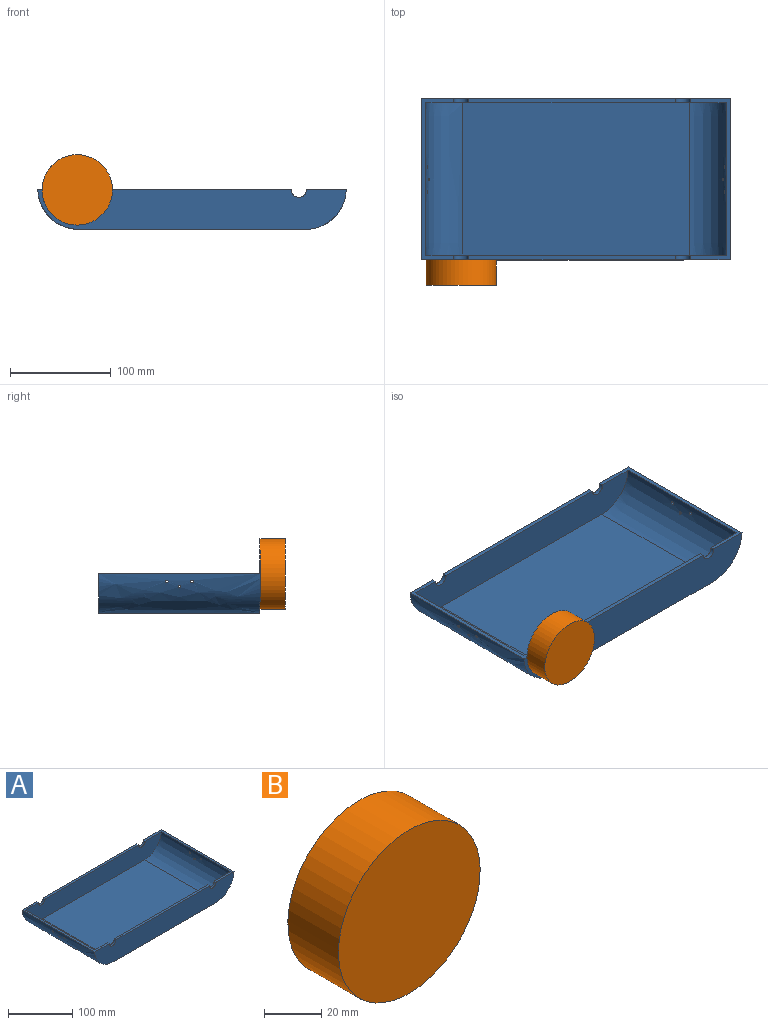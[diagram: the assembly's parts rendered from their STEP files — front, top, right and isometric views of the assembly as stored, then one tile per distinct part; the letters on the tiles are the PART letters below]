
ASSEMBLY  parts=2 mates=1
PART A: 24 faces, bbox 306.3x160.1x39.1 mm
  f0: cylinder r=7.5mm len=15mm, axis (0,-1,0), area 94mm2, adj f2,f7,f8,f13
  f1: cylinder r=7.5mm len=15mm, axis (0,-1,0), area 94mm2, adj f3,f7,f12,f17
  f2: plane 205.13x4.03mm, normal (0,0,1), area 820.5mm2, adj f0,f4,f8,f13
  f3: plane 205.13x4.03mm, normal (0,0,1), area 820.5mm2, adj f1,f5,f12,f17
  f4: cylinder r=7.5mm len=15mm, axis (0,-1,0), area 94.2mm2, adj f2,f6,f8,f13
  f5: cylinder r=7.5mm len=15mm, axis (0,-1,0), area 94.2mm2, adj f3,f6,f12,f17
  f6: plane 160.01x39.49mm, normal (0,0,1), area 924.2mm2, adj f4,f5,f8,f11,f12,f13,f16,f17
  f7: plane 160.01x31.69mm, normal (0,0,1), area 861.8mm2, adj f0,f1,f8,f9,f12,f13,f14,f17
  f8: plane 306.25x39.14mm, normal (0,1,0), area 11099.7mm2, adj f0,f2,f4,f6,f7,f9,f10,f11
  f9: extruded ~160.01x40.74mm, area 9968.4mm2, adj f7,f8,f10,f12,f21,f22,f23
  f10: plane 224.84x160.04mm, normal (0,0,-1), area 35970.4mm2, adj f8,f9,f11,f12
  f11: extruded ~160.01x40.74mm, area 9968.4mm2, adj f6,f8,f10,f12,f18,f19,f20
  f12: plane 306.25x39.14mm, normal (0,-1,0), area 11099.7mm2, adj f1,f3,f5,f6,f7,f9,f10,f11
  f13: plane 298.24x35.14mm, normal (0,-1,0), area 9726.1mm2, adj f0,f2,f4,f6,f7,f14,f15,f16
  f14: extruded ~152.01x36.74mm, area 8514mm2, adj f7,f13,f15,f17,f21,f22,f23
  f15: plane 224.84x152.04mm, normal (0,0,1), area 34171.9mm2, adj f13,f14,f16,f17
  f16: extruded ~152.01x36.74mm, area 8514mm2, adj f6,f13,f15,f17,f18,f19,f20
  f17: plane 298.24x35.14mm, normal (0,1,0), area 9726.2mm2, adj f1,f3,f5,f6,f7,f14,f15,f16
  f18: cylinder r=1.25mm len=4.73mm, axis (-1,0,0), area 32.3mm2, adj f11,f16
  f19: cylinder r=1.25mm len=5.28mm, axis (-1,0,0), area 33.8mm2, adj f11,f16
  f20: cylinder r=1.25mm len=4.73mm, axis (-1,0,0), area 32.3mm2, adj f11,f16
  f21: cylinder r=1.25mm len=4.73mm, axis (-1,0,0), area 32.3mm2, adj f9,f14
  f22: cylinder r=1.25mm len=5.28mm, axis (-1,0,0), area 33.8mm2, adj f9,f14
  f23: cylinder r=1.25mm len=4.73mm, axis (-1,0,0), area 32.3mm2, adj f9,f14
PART B: 3 faces, bbox 70x25x70 mm
  f0: cylinder r=35mm len=70mm, axis (0,1,0), area 5497.8mm2, adj f1,f2
  f1: plane 70x70mm, normal (0,-1,0), area 3848.5mm2, adj f0
  f2: plane 70x70mm, normal (0,1,0), area 3848.5mm2, adj f0
PLACE A t=(-394.12,23.11,-66.06)mm fixed
PLACE B rot(axis=(0,0,1),0deg) t=(78.95,22.02,4.56)mm
MATE parallel B.f0 <-> A.f0  axis (0,1,0) through (78.95,22.02,4.56)mm
